# Revit family: COR
name_source: partatom
category: Specialty Equipment
units: mm (PartAtom-declared; Revit-internal decimal feet)

## family parameters
Cut with Voids When Loaded = No
Host = Face
Part Type = Normal
Room Calculation Point = No
Round Connector Dimension = Use Diameter
Shared = No

## types (4) — shared parameters
ABAA Compliance = Yes
Assembly Code = C3020200
Default Elevation = 0"
Depth = 1 3/4"
Description = Watertight vertical-application expansion joint for walls.
Durometer Hardness of Silicone Coating (ASTM D2240) = Shore A: 25
Manufacturer = EMSEAL Joint Systems Ltd
Model = Seismic Colorseal
Movement (of Nominal Material Size) = +50% / -50%
Pick Resistance = No
Product Data URL = https://bit.ly
Product Documentation URL = https://bit.ly
Product Page URL = https://bit.ly
R Value Range (ASTM C518) = 2.1 per 1-inch (25mm) depth
Rate of Air Leakage (ASTM E283) = Passed
Seal Material Note = Seismic Colorseal is coated on the wall side with standard Sikasil WS-295 water-resistant silicone. Also available coated with a  paintable STPE sealant.
Single Bellow = Yes
Staining (ASTM C510) = None
Temperature Range (ASTM C711) = 185°F (85°C) to -40°F (-40°C)
Tensile Strength (ASTM D3574) = 18 psi min; 145 kPa
Type Image = EMSEAL-COR.jpg
URL = http://www.emseal.com

## per-type parameters (varying)
| type | Width |
| COR - .5 inches | 1/2" |
| COR - .75 inches | 3/4" |
| COR - 1 inches | 1" |
| COR - 1.25 inches | 1 1/4" |

## geometry (parser evidence)
native form markers: Sweep x2
no freeform markers — native parametric forms only
